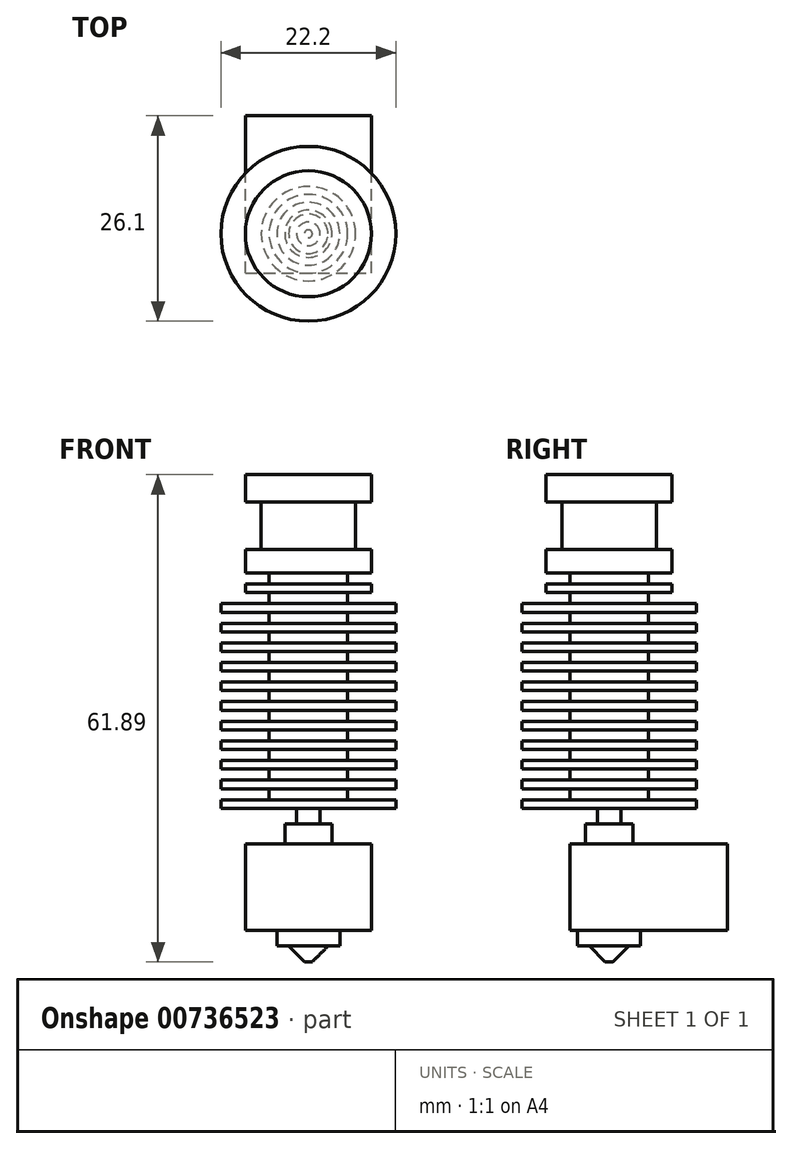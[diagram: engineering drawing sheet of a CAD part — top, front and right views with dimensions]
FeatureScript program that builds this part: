
annotation { "Feature Type Name" : "Feature", "Feature Type Description" : "" }
export const myFeature = defineFeature(function(context is Context, id is Id, definition is map)
    precondition{}
    {
        {
            var Q0;
            Q0=qCreatedBy(makeId("Front.planeOp"),FACE);
            var sketch = newSketch(context, id + "F0", { "sketchPlane" : qUnion([Q0])});
            skLineSegment(sketch, "E0", {"start": v(0, 38.75) * mm, "end": v(0, -39.42) * mm, "construction": true});
            skLineSegment(sketch, "E1", {"start": v(0, 24.95) * mm, "end": v(-8, 24.95) * mm});
            skLineSegment(sketch, "E2", {"start": v(-8, 24.95) * mm, "end": v(-8, 21.45) * mm});
            skLineSegment(sketch, "E3", {"start": v(-8, 21.45) * mm, "end": v(-6, 21.45) * mm});
            skLineSegment(sketch, "E4", {"start": v(-6, 21.45) * mm, "end": v(-6, 15.45) * mm});
            skLineSegment(sketch, "E5", {"start": v(-6, 15.45) * mm, "end": v(-8, 15.45) * mm});
            skLineSegment(sketch, "E6", {"start": v(-8, 15.45) * mm, "end": v(-8, 12.45) * mm});
            skLineSegment(sketch, "E7", {"start": v(-8, 12.45) * mm, "end": v(-5, 12.45) * mm});
            skLineSegment(sketch, "E8", {"start": v(-5, 12.45) * mm, "end": v(-5, 11.05) * mm});
            skLineSegment(sketch, "E9", {"start": v(-5, 11.05) * mm, "end": v(-8, 11.05) * mm});
            skLineSegment(sketch, "E10", {"start": v(-8, 11.05) * mm, "end": v(-8, 9.96) * mm});
            skLineSegment(sketch, "E11", {"start": v(-8, 9.96) * mm, "end": v(-5, 9.96) * mm});
            skLineSegment(sketch, "E12", {"start": v(-5, 9.96) * mm, "end": v(-5, 8.56) * mm});
            skLineSegment(sketch, "E13", {"start": v(-5, 8.56) * mm, "end": v(-11.1, 8.56) * mm});
            skLineSegment(sketch, "E14", {"start": v(-11.1, 8.56) * mm, "end": v(-11.1, 7.47) * mm});
            skLineSegment(sketch, "E15", {"start": v(-11.1, 7.47) * mm, "end": v(-5, 7.47) * mm});
            skLineSegment(sketch, "E16", {"start": v(-5, 7.47) * mm, "end": v(-5, 6.07) * mm});
            skLineSegment(sketch, "E17", {"start": v(-5, 6.07) * mm, "end": v(-11.1, 6.07) * mm});
            skLineSegment(sketch, "E18", {"start": v(-11.1, 6.07) * mm, "end": v(-11.1, 4.98) * mm});
            skLineSegment(sketch, "E19", {"start": v(-11.1, 4.98) * mm, "end": v(-5, 4.98) * mm});
            skLineSegment(sketch, "E20", {"start": v(-5, 4.98) * mm, "end": v(-5, 3.58) * mm});
            skLineSegment(sketch, "E21", {"start": v(-5, 3.58) * mm, "end": v(-11.1, 3.58) * mm});
            skLineSegment(sketch, "E22", {"start": v(-11.1, 3.58) * mm, "end": v(-11.1, 2.5) * mm});
            skLineSegment(sketch, "E23", {"start": v(-11.1, 2.5) * mm, "end": v(-5, 2.5) * mm});
            skLineSegment(sketch, "E24", {"start": v(-5, 2.5) * mm, "end": v(-5, 1.1) * mm});
            skLineSegment(sketch, "E25", {"start": v(-5, 1.1) * mm, "end": v(-11.1, 1.1) * mm});
            skLineSegment(sketch, "E26", {"start": v(-11.1, 1.1) * mm, "end": v(-11.1, 0) * mm});
            skLineSegment(sketch, "E27", {"start": v(-11.1, 0) * mm, "end": v(-5, 0) * mm});
            skLineSegment(sketch, "E28", {"start": v(-5, 0) * mm, "end": v(-5, -1.4) * mm});
            skLineSegment(sketch, "E29", {"start": v(-5, -1.4) * mm, "end": v(-11.1, -1.4) * mm});
            skLineSegment(sketch, "E30", {"start": v(-11.1, -1.4) * mm, "end": v(-11.1, -2.5) * mm});
            skLineSegment(sketch, "E31", {"start": v(-11.1, -2.5) * mm, "end": v(-5, -2.5) * mm});
            skLineSegment(sketch, "E32", {"start": v(-5, -2.5) * mm, "end": v(-5, -3.9) * mm});
            skLineSegment(sketch, "E33", {"start": v(-5, -3.9) * mm, "end": v(-11.1, -3.9) * mm});
            skLineSegment(sketch, "E34", {"start": v(-11.1, -3.9) * mm, "end": v(-11.1, -4.98) * mm});
            skLineSegment(sketch, "E35", {"start": v(-11.1, -4.98) * mm, "end": v(-5, -4.98) * mm});
            skLineSegment(sketch, "E36", {"start": v(-5, -4.98) * mm, "end": v(-5, -6.38) * mm});
            skLineSegment(sketch, "E37", {"start": v(-5, -6.38) * mm, "end": v(-11.1, -6.38) * mm});
            skLineSegment(sketch, "E38", {"start": v(-11.1, -6.38) * mm, "end": v(-11.1, -7.47) * mm});
            skLineSegment(sketch, "E39", {"start": v(-11.1, -7.47) * mm, "end": v(-5, -7.47) * mm});
            skLineSegment(sketch, "E40", {"start": v(-5, -7.47) * mm, "end": v(-5, -8.87) * mm});
            skLineSegment(sketch, "E41", {"start": v(-5, -8.87) * mm, "end": v(-11.1, -8.87) * mm});
            skLineSegment(sketch, "E42", {"start": v(-11.1, -8.87) * mm, "end": v(-11.1, -9.96) * mm});
            skLineSegment(sketch, "E43", {"start": v(-11.1, -9.96) * mm, "end": v(-5, -9.96) * mm});
            skLineSegment(sketch, "E44", {"start": v(-5, -9.96) * mm, "end": v(-5, -11.36) * mm});
            skLineSegment(sketch, "E45", {"start": v(-5, -11.36) * mm, "end": v(-11.1, -11.36) * mm});
            skLineSegment(sketch, "E46", {"start": v(-11.1, -11.36) * mm, "end": v(-11.1, -12.45) * mm});
            skLineSegment(sketch, "E47", {"start": v(-11.1, -12.45) * mm, "end": v(-5, -12.45) * mm});
            skLineSegment(sketch, "E48", {"start": v(-5, -12.45) * mm, "end": v(-5, -13.85) * mm});
            skLineSegment(sketch, "E49", {"start": v(-5, -13.85) * mm, "end": v(-11.1, -13.85) * mm});
            skLineSegment(sketch, "E50", {"start": v(-11.1, -13.85) * mm, "end": v(-11.1, -14.95) * mm});
            skLineSegment(sketch, "E51", {"start": v(-11.1, -14.95) * mm, "end": v(-5, -14.95) * mm});
            skLineSegment(sketch, "E52", {"start": v(-5, -14.95) * mm, "end": v(-5, -16.35) * mm});
            skLineSegment(sketch, "E53", {"start": v(-5, -16.35) * mm, "end": v(-11.1, -16.35) * mm});
            skLineSegment(sketch, "E54", {"start": v(-11.1, -16.35) * mm, "end": v(-11.1, -17.44) * mm});
            skLineSegment(sketch, "E55", {"start": v(-11.1, -17.44) * mm, "end": v(0, -17.44) * mm});
            skLineSegment(sketch, "E56", {"start": v(-1.5, -17.44) * mm, "end": v(-1.5, -19.44) * mm});
            skLineSegment(sketch, "E57", {"start": v(-1.5, -19.44) * mm, "end": v(-3, -19.44) * mm});
            skLineSegment(sketch, "E58", {"start": v(-3, -19.44) * mm, "end": v(-3, -32.94) * mm});
            skLineSegment(sketch, "E59", {"start": v(-3, -32.94) * mm, "end": v(-4, -32.94) * mm});
            skLineSegment(sketch, "E60", {"start": v(-4, -32.94) * mm, "end": v(-4, -34.94) * mm});
            skLineSegment(sketch, "E61", {"start": v(-4, -34.94) * mm, "end": v(-2.5, -34.94) * mm});
            skLineSegment(sketch, "E62", {"start": v(-2.5, -34.94) * mm, "end": v(-0.5, -36.94) * mm});
            skLineSegment(sketch, "E63", {"start": v(-0.5, -36.94) * mm, "end": v(0, -36.94) * mm});
            skLineSegment(sketch, "E64", {"start": v(0, -36.94) * mm, "end": v(0, -17.44) * mm});
            skLineSegment(sketch, "E65", {"start": v(0, 24.95) * mm, "end": v(0, -17.44) * mm});
            skSolve(sketch);
        }
        {
            var Q0;
            {var subQ0=sQuery(id+"F0.wireOp",EDGE,"E56");Q0=makeQuery(id+"F0.imprint","IMPRINT",FACE,{"disambiguationData":[TD([[makeQuery(id+"F0.imprint","IMPRINT",EDGE,{"derivedFrom":subQ0}),1.0]])]});}
            var Q1;
            Q1=makeQuery(id+"F0.imprint","IMPRINT",FACE,{"disambiguationData":[TD([[makeQuery(id+"F0.imprint","IMPRINT",EDGE,{"derivedFrom":sQuery(id+"F0.wireOp",EDGE,"E1")}),1.0]])]});
            var Q2;
            Q2=sQuery(id+"F0.wireOp",EDGE,"E0");
            revolve(context, id + "F1", {"entities" : qUnion([Q0, Q1]), "axis" : qUnion([Q2]), "revolveType" : RevolveType.FULL});
        }
        {
            var Q0;
            Q0=qCreatedBy(makeId("Front.planeOp"),FACE);
            var sketch = newSketch(context, id + "F2", { "sketchPlane" : qUnion([Q0])});
            skLineSegment(sketch, "E66.0", {"start": v(-3, -19.44) * mm, "end": v(-3, -32.94) * mm, "construction": true});
            skLineSegment(sketch, "E66.1", {"start": v(-1.5, -19.44) * mm, "end": v(-3, -19.44) * mm, "construction": true});
            skLineSegment(sketch, "E66.2", {"start": v(0, -36.94) * mm, "end": v(0, -17.44) * mm, "construction": true});
            skLineSegment(sketch, "E67.bottom", {"start": v(-8, -21.94) * mm, "end": v(8, -21.94) * mm});
            skLineSegment(sketch, "E67.top", {"start": v(-8, -32.94) * mm, "end": v(8, -32.94) * mm});
            skLineSegment(sketch, "E67.left", {"start": v(-8, -21.94) * mm, "end": v(-8, -32.94) * mm});
            skLineSegment(sketch, "E67.right", {"start": v(8, -21.94) * mm, "end": v(8, -32.94) * mm});
            skPoint(sketch, "E68", {"position": v(0, -21.94) * mm});
            skLineSegment(sketch, "E69.0", {"start": v(-3, -32.94) * mm, "end": v(3, -32.94) * mm, "construction": true});
            skSolve(sketch);
        }
        {
            var Q0;
            Q0=qSketchRegion(id+"F2",true);
            extrude(context, id + "F3", {"entities" : qUnion([Q0]), "operationType" : NewBodyOperationType.ADD, "depth" : 5 * mm, "hasSecondDirection" : true, "secondDirectionOppositeDirection" : true, "secondDirectionDepth" : 15 * mm});
        }
    });
